# Revit family: Zaniboni-Alba-Square_40°-1
name_source: partatom
category: Lighting Fixtures
revit_build: Autodesk Revit 2016 (Build: 20150220_1215(x64)
units: mm (PartAtom-declared; Revit-internal decimal feet)

## family parameters
Cut with Voids When Loaded = No
Host = Face
Light Source = Yes
Part Type = Normal
Room Calculation Point = No
Round Connector Dimension = Use Diameter
Shared = No

## types (3) — shared parameters
Assembly Code = E1020300
Beam = 24°
Body Finish = ZBN - Metal Matte White
CRI = 80
Color Filter = 16777215
Default Elevation = 48"
Dimming Lamp Color Temperature Shift = <None>
Emit Shape Visible in Rendering = No
Frame Finish = ZBN - Metal Matte White
Kelvin = 2700K
Keynote = 12500
Lamp D1 = 1 17/32"
Lamp D2 = 1 43/64"
Lamp Dist = 27/64"
Manufacturer = Zaniboni
Mechanism Finish = ZBN - Plastic-Black
Photometric Web File = generic
Screen Finish = ZBN - Glass
Support Finish = ZBN - Metal Matte White
Type Comments = Alba
URL = www.zanibonilighting.com
Voltage = 120 V
Wattage Comments = 7W
Width = 4 13/16"

## per-type parameters (varying)
| type | Body1 | Body2 | Description | Dist1 | Emit from Circle Diameter | Light D | Screen1 | Screen2 | Screen3 | Tilt Angle |
| D2-A3QWJ-0927A-2C-WS | Yes | No | 3 inch Edgeless Square Adjustable 40° Surface Mounted | 2 49/64" | 3" | 2 17/64" | No | Yes | No | 0.00° |
| D2-AL3QJ-0927A-2C-WS | Yes | No | 3 inch Edgeless Square Adjustable 40° Surface Mounted | 2 49/64" | 3" | 2 17/64" | Yes | No | No | 0.00° |
| D2-A3QPJ-0927A-2C-WS | No | Yes | 2 inch Edgeless Square Adjustable 40° Surface Mounted | 6 31/32" | 2" | 15/16" | No | No | Yes | 40.00° |

note: column(s) folded — value = type name in every type: Model

## geometry (parser evidence)
native form markers: Blend x2, Sweep x5
no freeform markers — native parametric forms only
